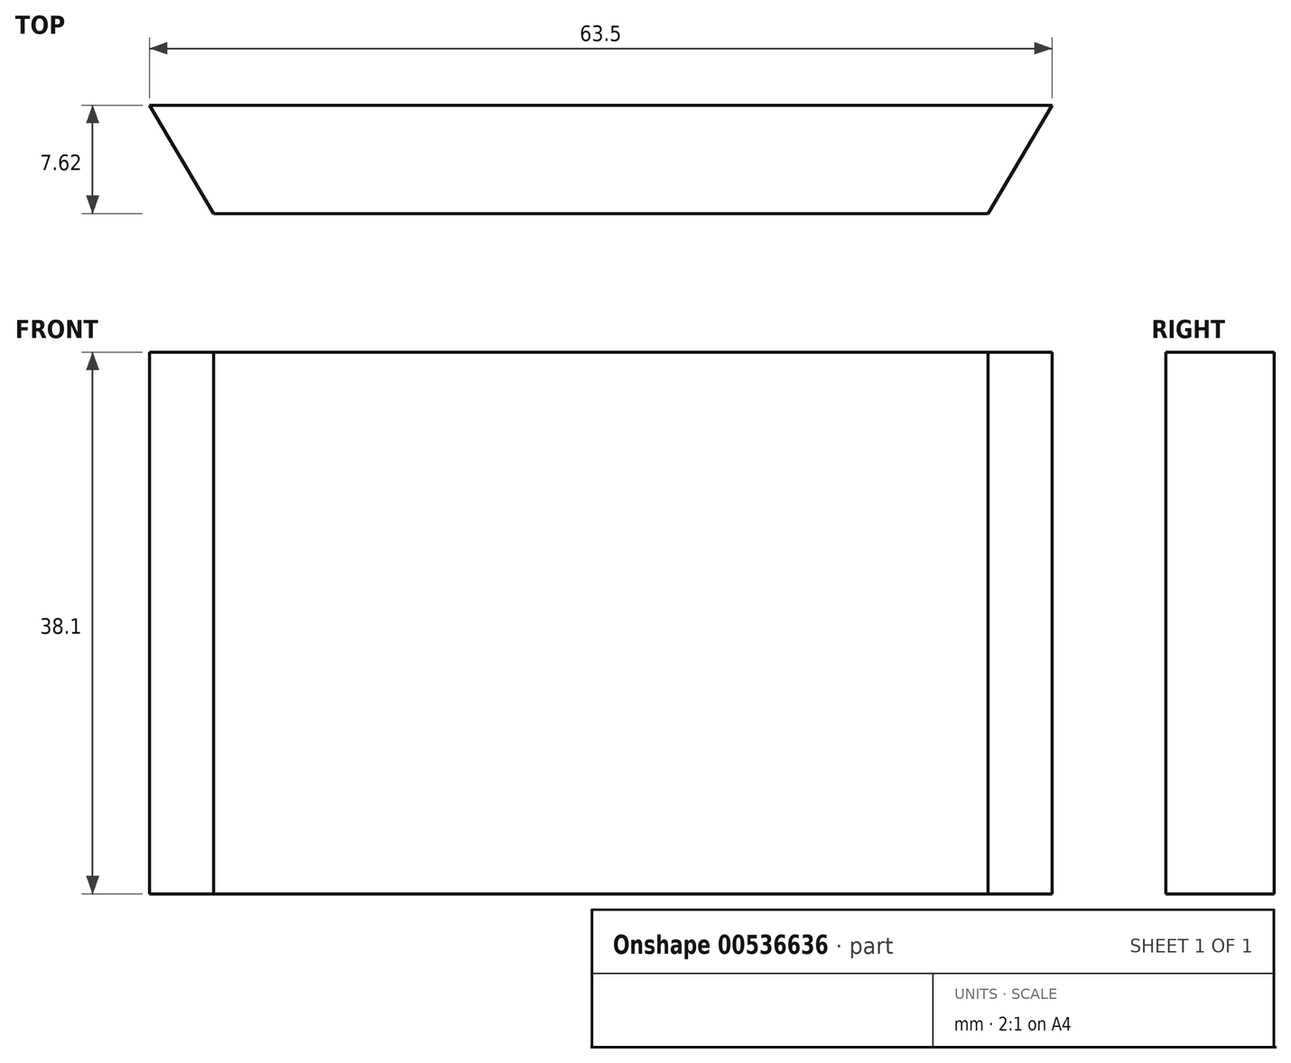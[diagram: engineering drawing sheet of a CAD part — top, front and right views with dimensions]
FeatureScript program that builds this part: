
annotation { "Feature Type Name" : "Feature", "Feature Type Description" : "" }
export const myFeature = defineFeature(function(context is Context, id is Id, definition is map)
    precondition{}
    {
        {
            var Q0;
            Q0=qCreatedBy(makeId("Front.planeOp"),FACE);
            var sketch = newSketch(context, id + "F0", { "sketchPlane" : qUnion([Q0])});
            skLineSegment(sketch, "E0.bottom", {"start": v(-23.28, 23.47) * mm, "end": v(8.47, 23.47) * mm});
            skLineSegment(sketch, "E0.top", {"start": v(-23.28, -14.63) * mm, "end": v(8.47, -14.63) * mm});
            skLineSegment(sketch, "E0.left", {"start": v(-23.28, 23.47) * mm, "end": v(-23.28, -14.63) * mm});
            skLineSegment(sketch, "E0.right", {"start": v(8.47, 23.47) * mm, "end": v(8.47, -14.63) * mm});
            skPoint(sketch, "E1.oppositeSnap0", {"position": v(-7.4, 23.47) * mm});
            skLineSegment(sketch, "E1.bottom", {"start": v(8.47, -14.63) * mm, "end": v(40.22, -14.63) * mm});
            skLineSegment(sketch, "E1.top", {"start": v(8.47, 23.47) * mm, "end": v(40.22, 23.47) * mm});
            skLineSegment(sketch, "E1.left", {"start": v(8.47, -14.63) * mm, "end": v(8.47, 23.47) * mm});
            skLineSegment(sketch, "E1.right", {"start": v(40.22, -14.63) * mm, "end": v(40.22, 23.47) * mm});
            skSolve(sketch);
        }
        {
            var Q0;
            Q0 = qSketchRegion(id + "F0", true);
            extrude(context, id + "F1", {"entities" : qUnion([Q0]), "depth" : 7.62 * mm, "offsetDistance" : 25.4 * mm});
        }
        {
            var Q0;
            Q0=makeQuery(id+"F1.opExtrude","SWEPT_FACE",FACE,{"disambiguationData":[OSD([sQuery(id+"F0.wireOp",EDGE,"E0.bottom"),sQuery(id+"F0.wireOp",EDGE,"E1.top")])]});
            var sketch = newSketch(context, id + "F2", { "sketchPlane" : qUnion([Q0])});
            skLineSegment(sketch, "E2", {"start": v(40.22, 0) * mm, "end": v(35.71, -7.62) * mm});
            skLineSegment(sketch, "E3", {"start": v(35.71, -7.62) * mm, "end": v(40.22, -7.62) * mm});
            skLineSegment(sketch, "E4", {"start": v(40.22, -7.62) * mm, "end": v(40.22, 0) * mm});
            skLineSegment(sketch, "E5.MirrorCS", {"start": v(-23.28, 0) * mm, "end": v(-18.78, -7.62) * mm});
            skLineSegment(sketch, "E6.MirrorCS", {"start": v(-23.28, -7.62) * mm, "end": v(-23.28, 0) * mm});
            skLineSegment(sketch, "E7.MirrorCS", {"start": v(-18.78, -7.62) * mm, "end": v(-23.28, -7.62) * mm});
            skSolve(sketch);
        }
        {
            var Q0;
            Q0 = qSketchRegion(id + "F2", true);
            extrude(context, id + "F3", {"entities" : qUnion([Q0]), "operationType" : NewBodyOperationType.REMOVE, "oppositeDirection" : true, "depth" : 38.58 * mm, "offsetDistance" : 25.4 * mm});
        }
    });
